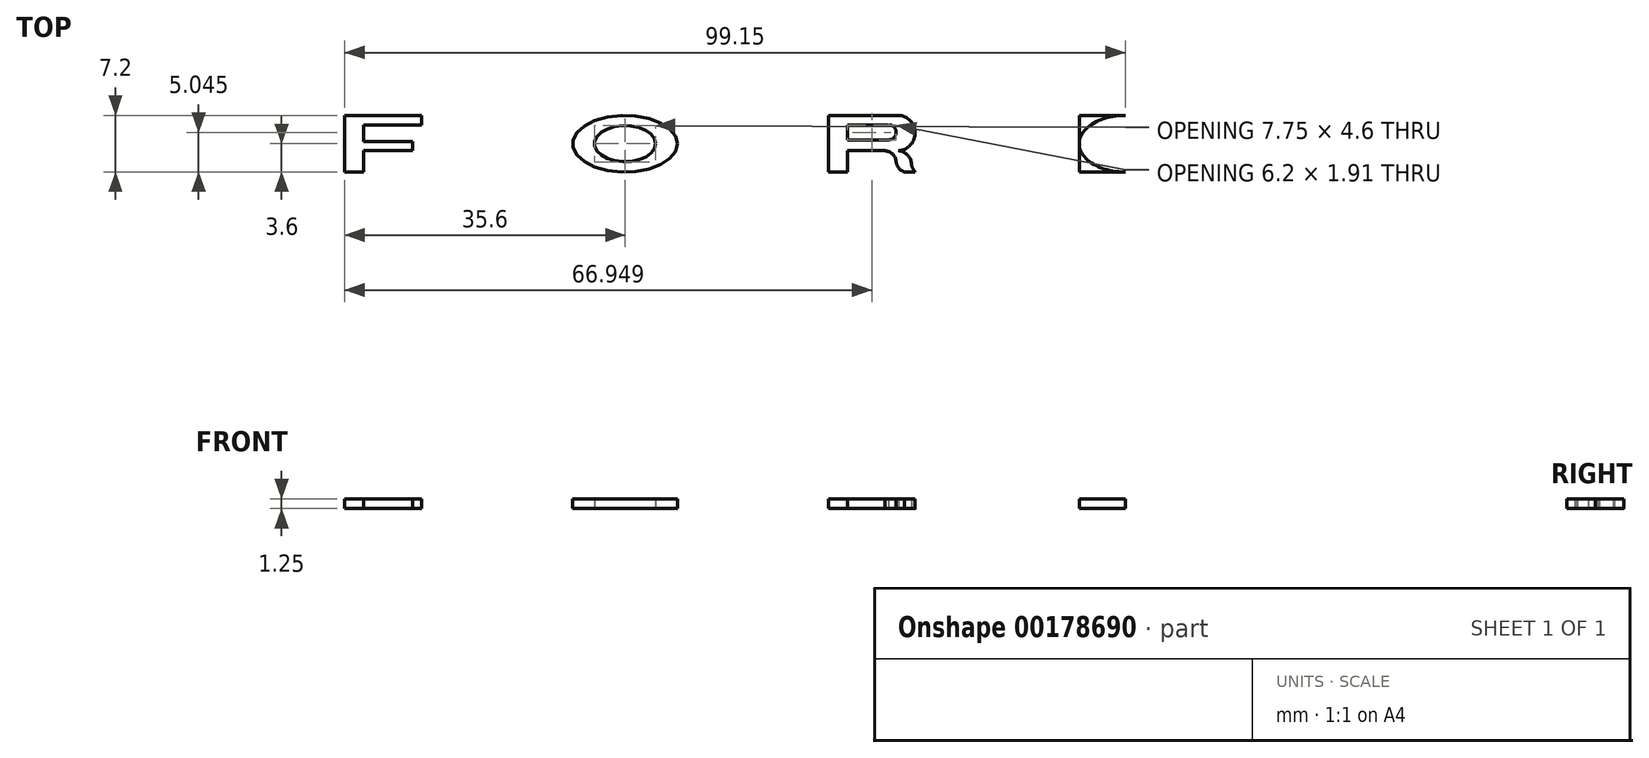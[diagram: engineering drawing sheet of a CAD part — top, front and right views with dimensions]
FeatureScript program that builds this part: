
annotation { "Feature Type Name" : "Feature", "Feature Type Description" : "" }
export const myFeature = defineFeature(function(context is Context, id is Id, definition is map)
    precondition{}
    {
        {
            var Q0;
            Q0=qCreatedBy(makeId("Top.planeOp"),FACE);
            var sketch = newSketch(context, id + "F0", { "sketchPlane" : qUnion([Q0])});
            skLineSegment(sketch, "E0.bottom", {"start": v(52.5, 3.6) * mm, "end": v(-52.5, 3.6) * mm});
            skLineSegment(sketch, "E0.top", {"start": v(52.5, -3.6) * mm, "end": v(-52.5, -3.6) * mm});
            skLineSegment(sketch, "E0.left", {"start": v(52.5, 3.6) * mm, "end": v(52.5, -3.6) * mm});
            skLineSegment(sketch, "E0.right", {"start": v(-52.5, 3.6) * mm, "end": v(-52.5, -3.6) * mm});
            skPoint(sketch, "E0.middle", {"position": v(0, 0) * mm});
            skSolve(sketch);
        }
        {
            var Q0;
            Q0=makeQuery(id+"F0.imprint","IMPRINT",FACE,{"disambiguationData":[TD([[makeQuery(id+"F0.imprint","IMPRINT",EDGE,{"derivedFrom":sQuery(id+"F0.wireOp",EDGE,"E0.bottom")}),1.0]])]});
            var sketch = newSketch(context, id + "F1", { "sketchPlane" : qUnion([Q0])});
            skLineSegment(sketch, "E1.0", {"start": v(-52.5, 3.6) * mm, "end": v(-52.5, -3.6) * mm});
            skLineSegment(sketch, "E2", {"start": v(-52.5, 3.6) * mm, "end": v(-42.75, 3.6) * mm});
            skLineSegment(sketch, "E3", {"start": v(-42.75, 3.6) * mm, "end": v(-42.75, 2.4) * mm});
            skLineSegment(sketch, "E4", {"start": v(-52.5, -3.6) * mm, "end": v(-50.1, -3.6) * mm});
            skLineSegment(sketch, "E5", {"start": v(-42.75, 2.4) * mm, "end": v(-50.1, 2.4) * mm});
            skLineSegment(sketch, "E6", {"start": v(-50.1, -3.6) * mm, "end": v(-50.1, -0.9) * mm});
            skLineSegment(sketch, "E7", {"start": v(-50.1, -0.9) * mm, "end": v(-43.9, -0.9) * mm});
            skLineSegment(sketch, "E8", {"start": v(-43.9, -0.9) * mm, "end": v(-43.9, 0.3) * mm});
            skLineSegment(sketch, "E9", {"start": v(-43.9, 0.3) * mm, "end": v(-50.1, 0.3) * mm});
            skLineSegment(sketch, "E10", {"start": v(-50.1, 0.3) * mm, "end": v(-50.1, 2.4) * mm});
            skSolve(sketch);
        }
        {
            var Q0;
            Q0=makeQuery(id+"F0.imprint","IMPRINT",FACE,{"disambiguationData":[TD([[makeQuery(id+"F0.imprint","IMPRINT",EDGE,{"derivedFrom":sQuery(id+"F0.wireOp",EDGE,"E0.bottom")}),1.0]])]});
            var sketch = newSketch(context, id + "F2", { "sketchPlane" : qUnion([Q0])});
            skLineSegment(sketch, "E11.0", {"start": v(-42.75, 3.6) * mm, "end": v(-42.75, 2.4) * mm});
            skPoint(sketch, "E12", {"position": v(-16.9, 0) * mm});
            skEllipse(sketch, "E13", {"center": v(-16.9, 0) * mm, "majorRadius": 3.88 * mm, "minorRadius": 2.3 * mm, "majorAxis": v(1, 0)});
            skEllipse(sketch, "E14", {"center": v(-16.9, 0) * mm, "majorRadius": 6.65 * mm, "minorRadius": 3.6 * mm, "majorAxis": v(1, 0)});
            skPoint(sketch, "E15.startSnap0", {"position": v(-10.25, 0) * mm});
            skPoint(sketch, "E15.endSnap0", {"position": v(-10.25, 0) * mm});
            skSolve(sketch);
        }
        {
            var Q0;
            {var subQ1=sQuery(id+"F1.wireOp",EDGE,"E3");Q0=makeQuery(id+"F1.imprint","IMPRINT",FACE,{"disambiguationData":[TD([[makeQuery(id+"F1.imprint","IMPRINT",EDGE,{"derivedFrom":subQ1}),1.0]])]});}
            var sketch = newSketch(context, id + "F3", { "sketchPlane" : qUnion([Q0])});
            skLineSegment(sketch, "E16", {"start": v(8.95, -3.6) * mm, "end": v(8.95, 3.6) * mm});
            skLineSegment(sketch, "E17", {"start": v(8.95, -3.6) * mm, "end": v(11.35, -3.6) * mm});
            skLineSegment(sketch, "E18", {"start": v(11.35, -3.6) * mm, "end": v(11.35, -0.9) * mm});
            skLineSegment(sketch, "E19", {"start": v(11.35, 2.4) * mm, "end": v(11.35, 0.5) * mm});
            skArc(sketch, "E20", {"start": v(17.55, -0.9) * mm, "mid": v(19.95, 1.35) * mm, "end": v(17.55, 3.6) * mm});
            skArc(sketch, "E21", {"start": v(16.56, 0.5) * mm, "mid": v(17.55, 1.45) * mm, "end": v(16.56, 2.4) * mm});
            skLineSegment(sketch, "E22", {"start": v(11.35, 2.4) * mm, "end": v(16.56, 2.4) * mm});
            skLineSegment(sketch, "E23", {"start": v(11.35, 0.5) * mm, "end": v(16.56, 0.5) * mm});
            skArc(sketch, "E24", {"start": v(17.55, -2.36) * mm, "mid": v(17.9, -3.11) * mm, "end": v(18.57, -3.6) * mm});
            skLineSegment(sketch, "E25", {"start": v(18.57, -3.6) * mm, "end": v(19.95, -3.6) * mm});
            skArc(sketch, "E26", {"start": v(17.55, -2.36) * mm, "mid": v(17.12, -1.34) * mm, "end": v(16.1, -0.9) * mm});
            skLineSegment(sketch, "E27", {"start": v(11.35, -0.9) * mm, "end": v(16.1, -0.9) * mm});
            skArc(sketch, "E28", {"start": v(19.49, -2.61) * mm, "mid": v(18.88, -1.34) * mm, "end": v(17.55, -0.9) * mm});
            skArc(sketch, "E29", {"start": v(19.49, -2.61) * mm, "mid": v(19.66, -3.13) * mm, "end": v(19.95, -3.6) * mm});
            skLineSegment(sketch, "E30", {"start": v(8.95, 3.6) * mm, "end": v(17.55, 3.6) * mm});
            skSolve(sketch);
        }
        {
            var Q0;
            Q0=makeQuery(id+"F0.imprint","IMPRINT",FACE,{"disambiguationData":[TD([[makeQuery(id+"F0.imprint","IMPRINT",EDGE,{"derivedFrom":sQuery(id+"F0.wireOp",EDGE,"E0.bottom")}),1.0]])]});
            var sketch = newSketch(context, id + "F4", { "sketchPlane" : qUnion([Q0])});
            skLineSegment(sketch, "E31", {"start": v(40.8, 3.6) * mm, "end": v(40.8, -3.6) * mm});
            skLineSegment(sketch, "E32", {"start": v(43.2, 2.4) * mm, "end": v(43.2, -2.4) * mm});
            skLineSegment(sketch, "E33", {"start": v(40.8, 0) * mm, "end": v(52.5, 0) * mm});
            skLineSegment(sketch, "E34", {"start": v(52.5, 0) * mm, "end": v(49.9, 0) * mm});
            skPoint(sketch, "E35", {"position": v(46.65, 0) * mm});
            skPoint(sketch, "E36", {"position": v(46.65, 3.6) * mm});
            skPoint(sketch, "E37", {"position": v(46.65, -3.6) * mm});
            skPoint(sketch, "E38", {"position": v(52.5, 0) * mm});
            skPoint(sketch, "E39", {"position": v(49.9, 0) * mm});
            skEllipse(sketch, "E40", {"center": v(46.65, 0) * mm, "majorRadius": 3.25 * mm, "minorRadius": 2.39 * mm, "majorAxis": v(1, 0)});
            skEllipse(sketch, "E41", {"center": v(46.65, 0) * mm, "majorRadius": 5.85 * mm, "minorRadius": 3.6 * mm, "majorAxis": v(1, 0)});
            skLineSegment(sketch, "E42", {"start": v(43.2, -2.4) * mm, "end": v(46.65, -2.39) * mm});
            skLineSegment(sketch, "E43", {"start": v(43.2, 2.4) * mm, "end": v(46.65, 2.39) * mm});
            skLineSegment(sketch, "E44", {"start": v(40.8, 3.6) * mm, "end": v(46.65, 3.6) * mm});
            skLineSegment(sketch, "E45", {"start": v(40.8, -3.6) * mm, "end": v(46.65, -3.6) * mm});
            skSolve(sketch);
        }
        {
            var Q0;
            {var subQ0=sQuery(id+"F4.wireOp",EDGE,"E45");Q0=makeQuery(id+"F4.imprint","IMPRINT",FACE,{"disambiguationData":[TD([[makeQuery(id+"F4.imprint","IMPRINT",EDGE,{"derivedFrom":subQ0}),-1.0]])]});}
            var Q1;
            {var subQ0=sQuery(id+"F4.wireOp",EDGE,"E44");Q1=makeQuery(id+"F4.imprint","IMPRINT",FACE,{"disambiguationData":[TD([[makeQuery(id+"F4.imprint","IMPRINT",EDGE,{"derivedFrom":subQ0}),1.0]])]});}
            var Q2;
            {var subQ0=sQuery(id+"F4.wireOp",EDGE,"E34");Q2=makeQuery(id+"F4.imprint","IMPRINT",FACE,{"disambiguationData":[TD([[makeQuery(id+"F4.imprint","IMPRINT",EDGE,{"derivedFrom":subQ0}),-1.0]])]});}
            var Q3;
            {var subQ6=sQuery(id+"F4.wireOp",EDGE,"E34");Q3=makeQuery(id+"F4.imprint","IMPRINT",FACE,{"disambiguationData":[TD([[makeQuery(id+"F4.imprint","IMPRINT",EDGE,{"derivedFrom":subQ6}),1.0]])]});}
            extrude(context, id + "F5", {"entities" : qUnion([Q0, Q1, Q2, Q3]), "depth" : 1.25 * mm});
        }
        {
            var Q0;
            Q0=qCreatedBy(makeId("Top.planeOp"),FACE);
            var sketch = newSketch(context, id + "F6", { "sketchPlane" : qUnion([Q0])});
            skLineSegment(sketch, "E46.0", {"start": v(8.95, -3.6) * mm, "end": v(8.95, 3.6) * mm});
            skLineSegment(sketch, "E47.0", {"start": v(8.95, -3.6) * mm, "end": v(11.35, -3.6) * mm});
            skLineSegment(sketch, "E48.0", {"start": v(11.35, -3.6) * mm, "end": v(11.35, -0.9) * mm});
            skLineSegment(sketch, "E49.0", {"start": v(11.35, -0.9) * mm, "end": v(16.1, -0.9) * mm});
            skLineSegment(sketch, "E50.0", {"start": v(11.35, 0.5) * mm, "end": v(16.56, 0.5) * mm});
            skPoint(sketch, "E51.0", {"position": v(11.35, 1.45) * mm});
            skLineSegment(sketch, "E52.0", {"start": v(11.35, 2.4) * mm, "end": v(16.56, 2.4) * mm});
            skLineSegment(sketch, "E53.0", {"start": v(11.35, 2.4) * mm, "end": v(11.35, 0.5) * mm});
            skArc(sketch, "E54.0", {"start": v(16.56, 0.5) * mm, "mid": v(17.55, 1.45) * mm, "end": v(16.56, 2.4) * mm});
            skArc(sketch, "E55.0", {"start": v(17.55, -0.9) * mm, "mid": v(19.95, 1.35) * mm, "end": v(17.55, 3.6) * mm});
            skArc(sketch, "E56.0", {"start": v(19.49, -2.61) * mm, "mid": v(18.88, -1.34) * mm, "end": v(17.55, -0.9) * mm});
            skLineSegment(sketch, "E57.0", {"start": v(18.57, -3.6) * mm, "end": v(19.95, -3.6) * mm});
            skArc(sketch, "E58.0", {"start": v(17.55, -2.36) * mm, "mid": v(17.9, -3.11) * mm, "end": v(18.57, -3.6) * mm});
            skArc(sketch, "E59.0", {"start": v(17.55, -2.36) * mm, "mid": v(17.12, -1.34) * mm, "end": v(16.1, -0.9) * mm});
            skLineSegment(sketch, "E60.0", {"start": v(8.95, 3.6) * mm, "end": v(17.55, 3.6) * mm});
            skArc(sketch, "E61.0", {"start": v(19.49, -2.61) * mm, "mid": v(19.66, -3.13) * mm, "end": v(19.95, -3.6) * mm});
            skSolve(sketch);
        }
        {
            var Q0;
            Q0 = qSketchRegion(id + "F6", true);
            extrude(context, id + "F7", {"entities" : qUnion([Q0]), "depth" : 1.25 * mm});
        }
        {
            var Q0;
            Q0=qCreatedBy(makeId("Top.planeOp"),FACE);
            var sketch = newSketch(context, id + "F8", { "sketchPlane" : qUnion([Q0])});
            skEllipse(sketch, "E62.0", {"center": v(-16.9, 0) * mm, "majorRadius": 3.88 * mm, "minorRadius": 2.3 * mm, "majorAxis": v(1, 0)});
            skEllipse(sketch, "E63.0", {"center": v(-16.9, 0) * mm, "majorRadius": 6.65 * mm, "minorRadius": 3.6 * mm, "majorAxis": v(1, 0)});
            skSolve(sketch);
        }
        {
            var Q0;
            Q0 = qSketchRegion(id + "F8", true);
            extrude(context, id + "F9", {"entities" : qUnion([Q0]), "depth" : 1.25 * mm});
        }
        {
            var Q0;
            Q0=qCreatedBy(makeId("Top.planeOp"),FACE);
            var sketch = newSketch(context, id + "F10", { "sketchPlane" : qUnion([Q0])});
            skLineSegment(sketch, "E64.0", {"start": v(-52.5, 3.6) * mm, "end": v(-42.75, 3.6) * mm});
            skLineSegment(sketch, "E65.0", {"start": v(-42.75, 3.6) * mm, "end": v(-42.75, 2.4) * mm});
            skLineSegment(sketch, "E66.0", {"start": v(-42.75, 2.4) * mm, "end": v(-50.1, 2.4) * mm});
            skLineSegment(sketch, "E67.0", {"start": v(-50.1, 0.3) * mm, "end": v(-50.1, 2.4) * mm});
            skLineSegment(sketch, "E68.0", {"start": v(-43.9, 0.3) * mm, "end": v(-50.1, 0.3) * mm});
            skLineSegment(sketch, "E69.0", {"start": v(-50.1, -0.9) * mm, "end": v(-43.9, -0.9) * mm});
            skLineSegment(sketch, "E70.0", {"start": v(-43.9, -0.9) * mm, "end": v(-43.9, 0.3) * mm});
            skLineSegment(sketch, "E71.0", {"start": v(-52.5, 3.6) * mm, "end": v(-52.5, -3.6) * mm});
            skLineSegment(sketch, "E72.0", {"start": v(-50.1, -3.6) * mm, "end": v(-50.1, -0.9) * mm});
            skLineSegment(sketch, "E73.0", {"start": v(-52.5, -3.6) * mm, "end": v(-50.1, -3.6) * mm});
            skSolve(sketch);
        }
        {
            var Q0;
            Q0 = qSketchRegion(id + "F10", true);
            extrude(context, id + "F11", {"entities" : qUnion([Q0]), "depth" : 1.25 * mm});
        }
    });
